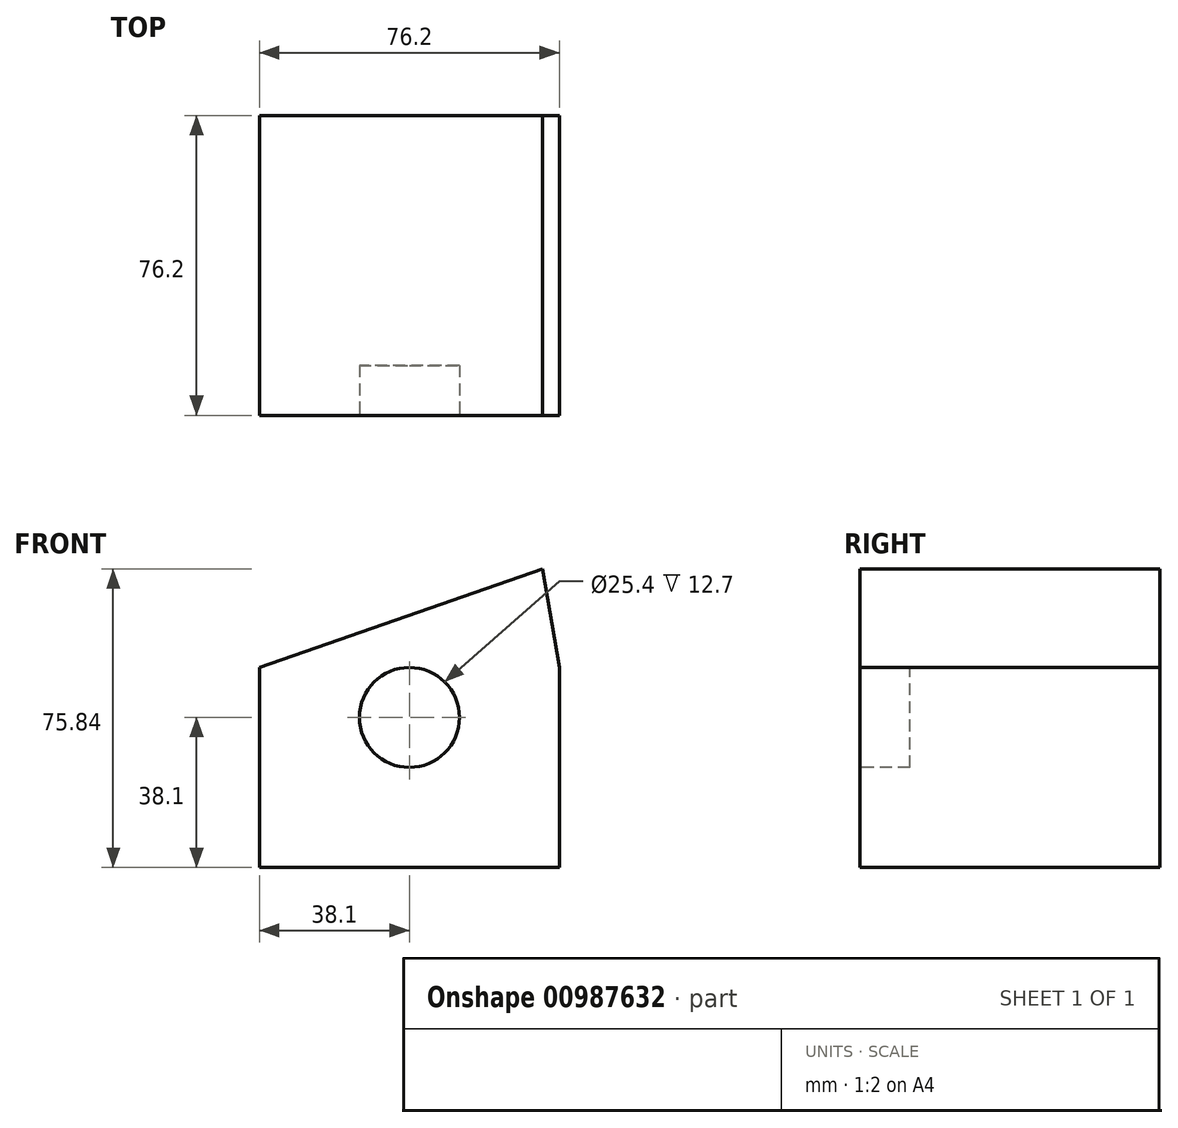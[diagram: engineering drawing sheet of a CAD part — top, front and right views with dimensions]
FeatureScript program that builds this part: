
annotation { "Feature Type Name" : "Feature", "Feature Type Description" : "" }
export const myFeature = defineFeature(function(context is Context, id is Id, definition is map)
    precondition{}
    {
        {
            var Q0;
            Q0=qCreatedBy(makeId("Front.planeOp"),FACE);
            var sketch = newSketch(context, id + "F0", { "sketchPlane" : qUnion([Q0])});
            skLineSegment(sketch, "E0.bottom", {"start": v(0, 0) * mm, "end": v(76.2, 0) * mm});
            skLineSegment(sketch, "E0.top", {"start": v(0, 50.8) * mm, "end": v(76.2, 50.8) * mm});
            skLineSegment(sketch, "E0.left", {"start": v(0, 0) * mm, "end": v(0, 50.8) * mm});
            skLineSegment(sketch, "E0.right", {"start": v(76.2, 0) * mm, "end": v(76.2, 50.8) * mm});
            skLineSegment(sketch, "E1", {"start": v(0, 50.8) * mm, "end": v(71.97, 75.84) * mm});
            skLineSegment(sketch, "E2", {"start": v(71.97, 75.84) * mm, "end": v(76.2, 50.8) * mm});
            skSolve(sketch);
        }
        {
            var Q0;
            Q0 = qSketchRegion(id + "F0", true);
            extrude(context, id + "F1", {"entities" : qUnion([Q0]), "depth" : 76.2 * mm, "offsetDistance" : 25.4 * mm});
        }
        {
            var Q0;
            Q0=makeQuery(id+"F1.opExtrude","CAP_FACE",FACE,{"disambiguationData":[OSD([sQuery(id+"F0.wireOp",EDGE,"E0.bottom"),sQuery(id+"F0.wireOp",EDGE,"E0.left"),sQuery(id+"F0.wireOp",EDGE,"E0.right"),sQuery(id+"F0.wireOp",EDGE,"E1"),sQuery(id+"F0.wireOp",EDGE,"E2")])],"isStart":false});
            var sketch = newSketch(context, id + "F2", { "sketchPlane" : qUnion([Q0])});
            skCircle(sketch, "E3", {"center": v(38.1, 38.1) * mm, "radius": 12.7 * mm});
            skSolve(sketch);
        }
        {
            var Q0;
            Q0 = qSketchRegion(id + "F2", true);
            extrude(context, id + "F3", {"entities" : qUnion([Q0]), "operationType" : NewBodyOperationType.REMOVE, "oppositeDirection" : true, "depth" : 12.7 * mm, "offsetDistance" : 25.4 * mm});
        }
    });
